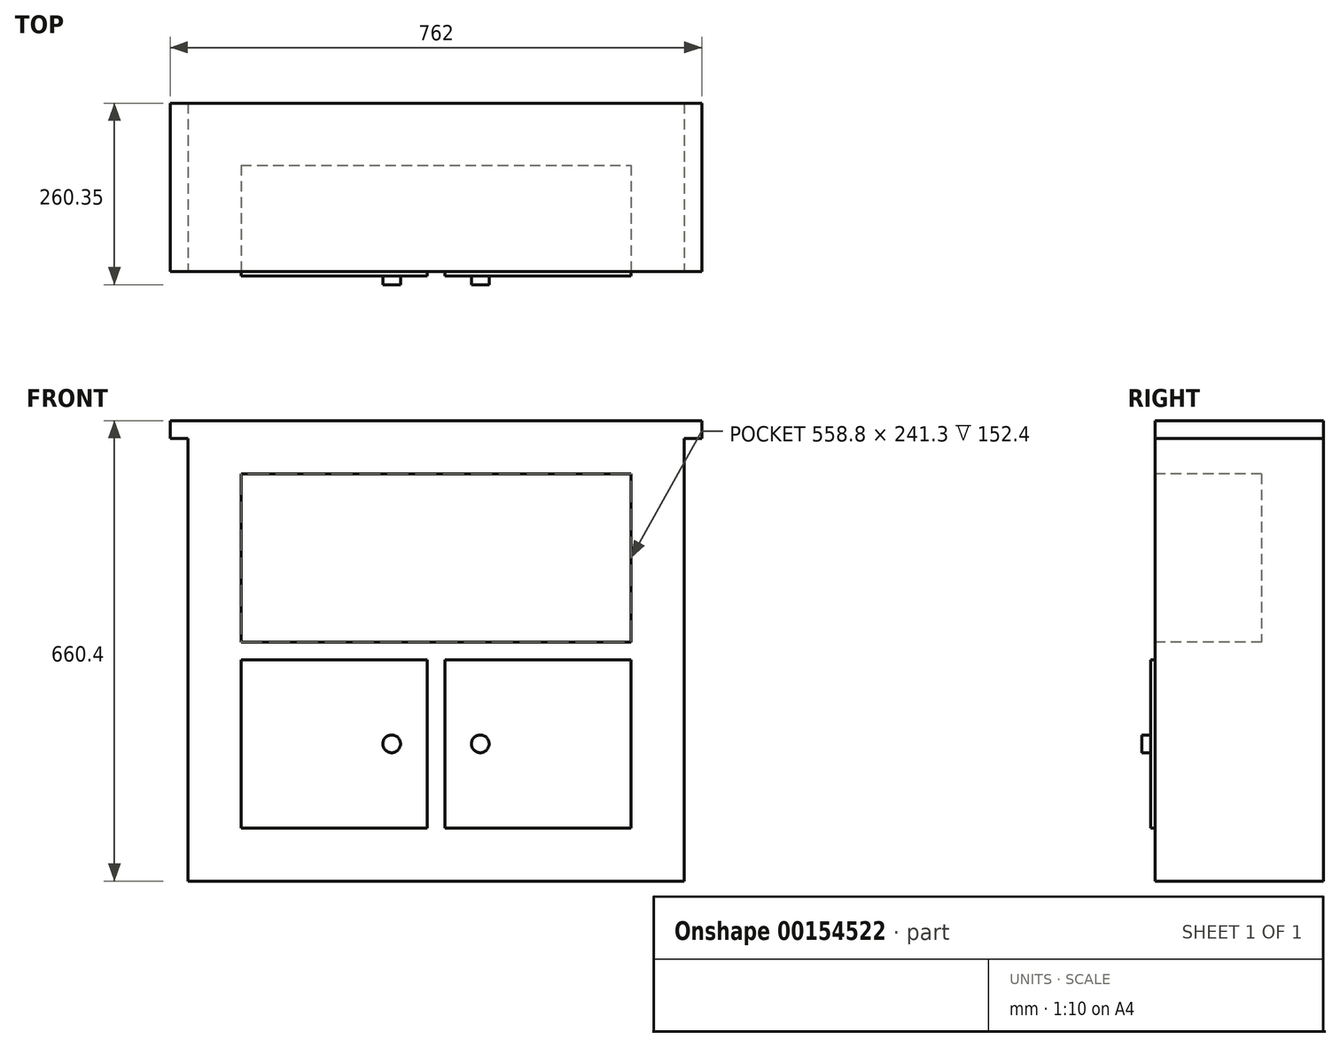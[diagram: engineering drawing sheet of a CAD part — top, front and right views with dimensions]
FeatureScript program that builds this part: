
annotation { "Feature Type Name" : "Feature", "Feature Type Description" : "" }
export const myFeature = defineFeature(function(context is Context, id is Id, definition is map)
    precondition{}
    {
        {
            var Q0;
            Q0=qCreatedBy(makeId("Front.planeOp"),FACE);
            var sketch = newSketch(context, id + "F0", { "sketchPlane" : qUnion([Q0])});
            skLineSegment(sketch, "E0.bottom", {"start": v(0, 0) * mm, "end": v(711.2, 0) * mm});
            skLineSegment(sketch, "E0.top", {"start": v(0, 635) * mm, "end": v(711.2, 635) * mm});
            skLineSegment(sketch, "E0.left", {"start": v(0, 0) * mm, "end": v(0, 635) * mm});
            skLineSegment(sketch, "E0.right", {"start": v(711.2, 0) * mm, "end": v(711.2, 635) * mm});
            skLineSegment(sketch, "E1.bottom", {"start": v(-25.4, 660.4) * mm, "end": v(736.6, 660.4) * mm});
            skLineSegment(sketch, "E1.top", {"start": v(-25.4, 635) * mm, "end": v(736.6, 635) * mm});
            skLineSegment(sketch, "E1.left", {"start": v(-25.4, 660.4) * mm, "end": v(-25.4, 635) * mm});
            skLineSegment(sketch, "E1.right", {"start": v(736.6, 660.4) * mm, "end": v(736.6, 635) * mm});
            skLineSegment(sketch, "E2", {"start": v(355.6, 660.4) * mm, "end": v(355.6, 0) * mm, "construction": true});
            skLineSegment(sketch, "E3.bottom", {"start": v(76.2, 584.2) * mm, "end": v(635, 584.2) * mm});
            skLineSegment(sketch, "E3.top", {"start": v(76.2, 342.9) * mm, "end": v(635, 342.9) * mm});
            skLineSegment(sketch, "E3.left", {"start": v(76.2, 584.2) * mm, "end": v(76.2, 342.9) * mm});
            skLineSegment(sketch, "E3.right", {"start": v(635, 584.2) * mm, "end": v(635, 342.9) * mm});
            skLineSegment(sketch, "E4.bottom", {"start": v(635, 317.5) * mm, "end": v(368.3, 317.5) * mm});
            skLineSegment(sketch, "E4.top", {"start": v(635, 76.2) * mm, "end": v(368.3, 76.2) * mm});
            skLineSegment(sketch, "E4.left", {"start": v(635, 317.5) * mm, "end": v(635, 76.2) * mm});
            skLineSegment(sketch, "E4.right", {"start": v(368.3, 317.5) * mm, "end": v(368.3, 76.2) * mm});
            skLineSegment(sketch, "E5.bottom", {"start": v(342.9, 317.5) * mm, "end": v(76.2, 317.5) * mm});
            skLineSegment(sketch, "E5.top", {"start": v(342.9, 76.2) * mm, "end": v(76.2, 76.2) * mm});
            skLineSegment(sketch, "E5.left", {"start": v(342.9, 317.5) * mm, "end": v(342.9, 76.2) * mm});
            skLineSegment(sketch, "E5.right", {"start": v(76.2, 317.5) * mm, "end": v(76.2, 76.2) * mm});
            skLineSegment(sketch, "E6", {"start": v(342.9, 196.85) * mm, "end": v(292.1, 196.85) * mm, "construction": true});
            skLineSegment(sketch, "E7", {"start": v(368.3, 196.85) * mm, "end": v(419.1, 196.85) * mm, "construction": true});
            skCircle(sketch, "E8", {"center": v(419.1, 196.85) * mm, "radius": 12.7 * mm});
            skCircle(sketch, "E9", {"center": v(292.1, 196.85) * mm, "radius": 12.7 * mm});
            skSolve(sketch);
        }
        {
            var Q0;
            Q0=makeQuery(id+"F0.imprint","IMPRINT",FACE,{"disambiguationData":[TD([[makeQuery(id+"F0.imprint","IMPRINT",EDGE,{"derivedFrom":sQuery(id+"F0.wireOp",EDGE,"E0.bottom")}),1.0]])]});
            var Q1;
            Q1=makeQuery(id+"F0.imprint","IMPRINT",FACE,{"disambiguationData":[TD([[makeQuery(id+"F0.imprint","IMPRINT",EDGE,{"derivedFrom":sQuery(id+"F0.wireOp",EDGE,"E1.bottom")}),-1.0]])]});
            var Q2;
            Q2=makeQuery(id+"F0.imprint","IMPRINT",FACE,{"disambiguationData":[TD([[makeQuery(id+"F0.imprint","IMPRINT",EDGE,{"derivedFrom":sQuery(id+"F0.wireOp",EDGE,"E5.bottom")}),1.0]])]});
            var Q3;
            Q3=makeQuery(id+"F0.imprint","IMPRINT",FACE,{"disambiguationData":[TD([[makeQuery(id+"F0.imprint","IMPRINT",EDGE,{"derivedFrom":sQuery(id+"F0.wireOp",EDGE,"E4.bottom")}),1.0]])]});
            var Q4;
            Q4=makeQuery(id+"F0.imprint","IMPRINT",FACE,{"disambiguationData":[TD([[makeQuery(id+"F0.imprint","IMPRINT",EDGE,{"derivedFrom":sQuery(id+"F0.wireOp",EDGE,"E8")}),1.0]])]});
            var Q5;
            Q5=makeQuery(id+"F0.imprint","IMPRINT",FACE,{"disambiguationData":[TD([[makeQuery(id+"F0.imprint","IMPRINT",EDGE,{"derivedFrom":sQuery(id+"F0.wireOp",EDGE,"E9")}),1.0]])]});
            var Q6;
            Q6=makeQuery(id+"F0.imprint","IMPRINT",FACE,{"disambiguationData":[TD([[makeQuery(id+"F0.imprint","IMPRINT",EDGE,{"derivedFrom":sQuery(id+"F0.wireOp",EDGE,"E3.bottom")}),-1.0]])]});
            extrude(context, id + "F1", {"entities" : qUnion([Q0, Q1, Q2, Q3, Q4, Q5, Q6]), "oppositeDirection" : true, "depth" : 241.3 * mm});
        }
        {
            var Q0;
            Q0=makeQuery(id+"F0.imprint","IMPRINT",FACE,{"disambiguationData":[TD([[makeQuery(id+"F0.imprint","IMPRINT",EDGE,{"derivedFrom":sQuery(id+"F0.wireOp",EDGE,"E3.bottom")}),-1.0]])]});
            extrude(context, id + "F2", {"entities" : qUnion([Q0]), "operationType" : NewBodyOperationType.REMOVE, "oppositeDirection" : true, "depth" : 152.4 * mm});
        }
        {
            var Q0;
            Q0=makeQuery(id+"F0.imprint","IMPRINT",FACE,{"disambiguationData":[TD([[makeQuery(id+"F0.imprint","IMPRINT",EDGE,{"derivedFrom":sQuery(id+"F0.wireOp",EDGE,"E5.bottom")}),1.0]])]});
            var Q1;
            Q1=makeQuery(id+"F0.imprint","IMPRINT",FACE,{"disambiguationData":[TD([[makeQuery(id+"F0.imprint","IMPRINT",EDGE,{"derivedFrom":sQuery(id+"F0.wireOp",EDGE,"E4.bottom")}),1.0]])]});
            var Q2;
            Q2=makeQuery(id+"F0.imprint","IMPRINT",FACE,{"disambiguationData":[TD([[makeQuery(id+"F0.imprint","IMPRINT",EDGE,{"derivedFrom":sQuery(id+"F0.wireOp",EDGE,"E8")}),1.0]])]});
            var Q3;
            Q3=makeQuery(id+"F0.imprint","IMPRINT",FACE,{"disambiguationData":[TD([[makeQuery(id+"F0.imprint","IMPRINT",EDGE,{"derivedFrom":sQuery(id+"F0.wireOp",EDGE,"E9")}),1.0]])]});
            extrude(context, id + "F3", {"entities" : qUnion([Q0, Q1, Q2, Q3]), "operationType" : NewBodyOperationType.ADD, "depth" : 6.35 * mm});
        }
        {
            var Q0;
            Q0=makeQuery(id+"F0.imprint","IMPRINT",FACE,{"disambiguationData":[TD([[makeQuery(id+"F0.imprint","IMPRINT",EDGE,{"derivedFrom":sQuery(id+"F0.wireOp",EDGE,"E8")}),1.0]])]});
            var Q1;
            Q1=makeQuery(id+"F0.imprint","IMPRINT",FACE,{"disambiguationData":[TD([[makeQuery(id+"F0.imprint","IMPRINT",EDGE,{"derivedFrom":sQuery(id+"F0.wireOp",EDGE,"E9")}),1.0]])]});
            var Q2;
            Q2=sQuery(id+"F0.wireOp",EDGE,"E9");
            var Q3;
            Q3=sQuery(id+"F0.wireOp",EDGE,"E8");
            extrude(context, id + "F4", {"entities" : qUnion([Q0, Q1]), "operationType" : NewBodyOperationType.ADD, "surfaceEntities" : qUnion([Q2, Q3]), "depth" : 19.05 * mm});
        }
    });
